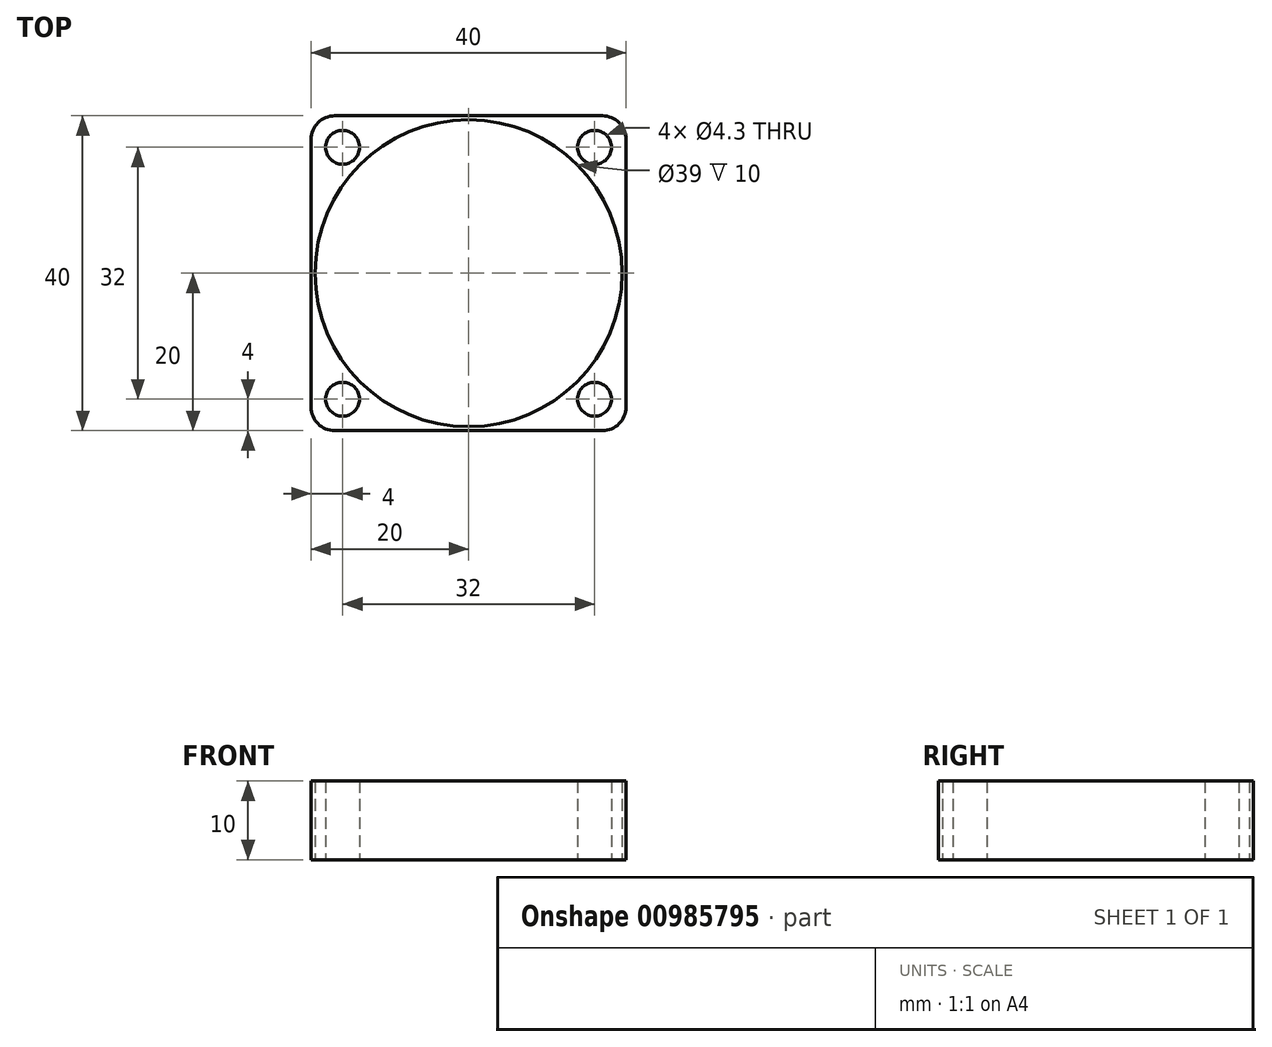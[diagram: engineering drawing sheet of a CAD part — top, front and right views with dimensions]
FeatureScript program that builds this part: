
annotation { "Feature Type Name" : "Feature", "Feature Type Description" : "" }
export const myFeature = defineFeature(function(context is Context, id is Id, definition is map)
    precondition{}
    {
        {
            var Q0;
            Q0=qCreatedBy(makeId("Top.planeOp"),FACE);
            var sketch = newSketch(context, id + "F0", { "sketchPlane" : qUnion([Q0])});
            skLineSegment(sketch, "E0.bottom", {"start": v(0, 0) * mm, "end": v(-40, 0) * mm});
            skLineSegment(sketch, "E0.top", {"start": v(0, 40) * mm, "end": v(-40, 40) * mm});
            skLineSegment(sketch, "E0.left", {"start": v(0, 0) * mm, "end": v(0, 40) * mm});
            skLineSegment(sketch, "E0.right", {"start": v(-40, 0) * mm, "end": v(-40, 40) * mm});
            skLineSegment(sketch, "E1", {"start": v(0, 40) * mm, "end": v(-40, 0) * mm, "construction": true});
            skLineSegment(sketch, "E2", {"start": v(-40, 40) * mm, "end": v(0, 0) * mm, "construction": true});
            skCircle(sketch, "E3", {"center": v(-20, 20) * mm, "radius": 19.5 * mm});
            skCircle(sketch, "E4", {"center": v(-36, 36) * mm, "radius": 2.15 * mm});
            skCircle(sketch, "E5", {"center": v(-4, 4) * mm, "radius": 2.15 * mm});
            skCircle(sketch, "E6", {"center": v(-36, 4) * mm, "radius": 2.15 * mm});
            skCircle(sketch, "E7", {"center": v(-4, 36) * mm, "radius": 2.15 * mm});
            skSolve(sketch);
        }
        {
            var Q0;
            Q0=makeQuery(id+"F0.imprint","IMPRINT",FACE,{"disambiguationData":[TD([[makeQuery(id+"F0.imprint","IMPRINT",EDGE,{"derivedFrom":sQuery(id+"F0.wireOp",EDGE,"E0.bottom")}),-1.0]])]});
            extrude(context, id + "F1", {"entities" : qUnion([Q0]), "depth" : 10 * mm, "offsetDistance" : 25 * mm});
        }
        {
            var Q0;
            Q0=makeQuery(id+"F1.opExtrude","SWEPT_EDGE",EDGE,{"disambiguationData":[OSD([sQuery(id+"F0.wireOp",EDGE,"E0.bottom"),sQuery(id+"F0.wireOp",EDGE,"E0.left")])]});
            var Q1;
            Q1=makeQuery(id+"F1.opExtrude","SWEPT_EDGE",EDGE,{"disambiguationData":[OSD([sQuery(id+"F0.wireOp",EDGE,"E0.top"),sQuery(id+"F0.wireOp",EDGE,"E0.left")])]});
            var Q2;
            Q2=makeQuery(id+"F1.opExtrude","SWEPT_EDGE",EDGE,{"disambiguationData":[OSD([sQuery(id+"F0.wireOp",EDGE,"E0.top"),sQuery(id+"F0.wireOp",EDGE,"E0.right")])]});
            var Q3;
            Q3=makeQuery(id+"F1.opExtrude","SWEPT_EDGE",EDGE,{"disambiguationData":[OSD([sQuery(id+"F0.wireOp",EDGE,"E0.bottom"),sQuery(id+"F0.wireOp",EDGE,"E0.right")])]});
            fillet(context, id + "F2", {"entities" : qUnion([Q0, Q1, Q2, Q3]), "tangentPropagation" : true, "radius" : 3 * mm, "defaultsChanged" : true, "vertexSettings" : [], "allowEdgeOverflow" : false});
        }
    });
